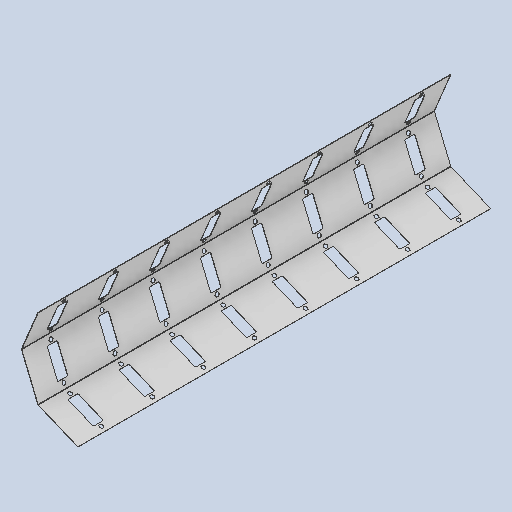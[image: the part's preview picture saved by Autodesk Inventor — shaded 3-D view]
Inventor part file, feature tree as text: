
AUTODESK INVENTOR PART (.ipt)
format: ipt  version: 2025 (Build 290162010, 162A)  size: 965,632 bytes
history: native  units: mm
features: sheet_metal_op x3, sketch x3, other x2, extrude x1, fillet x1, pattern_circular x1, pattern_linear x1, chamfer x1, projected_geometry x1
ambient origin geometry x8: Origin, YZ Plane, XZ Plane, XY Plane, X Axis, Y Axis, Z Axis, Center Point
bodies: Body1 (feature_tree)
feature tree (14):
  sheet_metal_op  "Contour Flange3"
  extrude  "Extrusion4"  Depth=4.0mm
  fillet  "Fillet1"  Radius=0.9mm
  pattern_circular  "Circular Pattern2"  [2 undecoded]
  pattern_linear  "Rectangular Pattern2"  Spacing1=2.0mm  [1 undecoded]
  chamfer  "Corner Round1"
  sketch  "Sketch2"  dims[d58=4.0mm d59=4.0mm d70=0.9mm]
  other  "Plate6"
  sheet_metal_op  "Bend6"
  sheet_metal_op  "Corner6"
  sketch  "Sketch11"  dims[d72=0.9mm]
  projected_geometry  "Projected Loop1"
  other  "Definition1"
  sketch  "Sketch11:Copy"  dims[d74=513.0mm d75=2.0mm d76=2.0mm d77=1.0mm d78=4.0mm d79=2.0mm d80=2020.0mm d81=2.0mm d82=3.0mm d83=8.0mm d84=2.0mm d85=2.0mm d141=50.0mm d142=135.0mm d145=125.0mm d147=10.0mm d148=0.0mm d149=5.0mm d150=30.0mm d151=90.0deg d153=80.0mm d155=250.0mm d156=2.0mm d157=206.278354mm d159=16.8mm d160=16.8mm d161=165.0mm]
note: 3 required parameter values undecoded (feature->parameter linkage not recoverable at this tier; creation-order binding heuristic only, values carry confidence <= 0.55)
